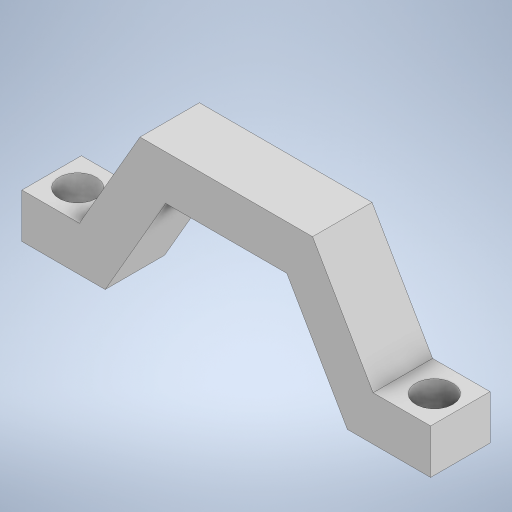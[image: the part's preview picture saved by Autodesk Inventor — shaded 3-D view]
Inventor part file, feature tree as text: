
AUTODESK INVENTOR PART (.ipt)
format: ipt  version: 2023.1 (Build 271208000, 208)  size: 245,248 bytes
history: native  units: mm
features: extrude x2, sketch x2, other x1
ambient origin geometry x8: Origin, YZ Plane, XZ Plane, XY Plane, X Axis, Y Axis, Z Axis, Center Point
bodies: Body1 (feature_tree)
feature tree (5):
  other  "솔리드1"
  extrude  "돌출1"  Depth=27.5mm
  extrude  "돌출2"  Depth=16.3mm
  sketch  "스케치1"
  sketch  "스케치2"
